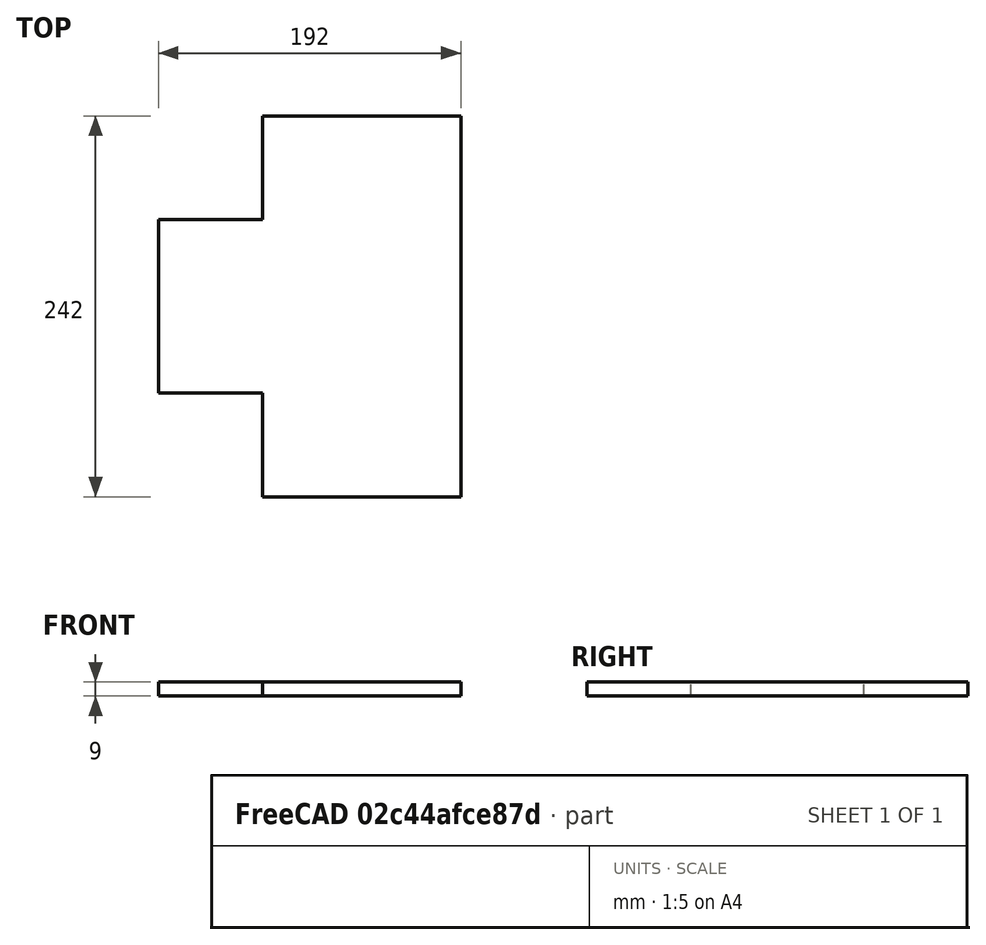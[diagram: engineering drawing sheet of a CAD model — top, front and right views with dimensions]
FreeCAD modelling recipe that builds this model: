
FCSTD DOCUMENT  (FreeCAD 0.16RUnknown)
Label: plaque_bas
License: All rights reserved
LicenseURL: http://en.wikipedia.org/wiki/All_rights_reserved
objects: App::FeaturePython×6, App::DocumentObjectGroup×4, Drawing::FeatureViewPart×4, Part::Plane×3, Drawing::FeatureViewPython×3, Part::Fuse×1, Part::Cut×1, Part::FeaturePython×1, Part::Extrusion×1, Drawing::FeaturePage×1
note: 7 computed .brp shape members not serialized (recipe doc carries the construction recipe); baked Part::Feature solids carry a one-line shape summary decoded from their .brp

FEATURE [Part::Plane] square
  Length = 192
  Placement = pos=(9,-121,0) rot=(0,0,1;0rad)
  Width = 242
FEATURE [Part::Plane] square001
  Length = 75
  Placement = pos=(0,55,0) rot=(0,0,1;0rad)
  Width = 75
FEATURE [Part::Plane] square002
  Length = 75
  Placement = pos=(0,-130,0) rot=(0,0,1;0rad)
  Width = 75
FEATURE [Part::Fuse] union
  Base = -> square001
  Tool = -> square002
FEATURE [Part::Cut] difference
  Base = -> square
  Tool = -> union
FEATURE [Part::FeaturePython] RefineLinearExtrude  # WARN: FeaturePython — macro-defined, semantics opaque (R4)
  Base = -> difference
FEATURE [Part::Extrusion] LinearExtrude
  Base = -> RefineLinearExtrude
  Dir = (0,0,9)
  Solid = true
FEATURE [App::FeaturePython] Dimension  # Draft dimension (typed FeaturePython)
  Dimline = (0,127,0)
  Direction = (0,0,0)
  Distance = 192
  End = (201,121,0)
  Normal = (0,0,1)
  Start = (9,121,0)
FEATURE [App::FeaturePython] Dimension001  # Draft dimension (typed FeaturePython)
  Dimline = (207,0,0)
  Direction = (0,0,0)
  Distance = 242
  End = (201,-121,0)
  Normal = (0,0,1)
  Start = (201,121,0)
FEATURE [App::DocumentObjectGroup] Groupe  label="XY"
  Group = -> [Dimension,Dimension001]
FEATURE [App::FeaturePython] Dimension002  # Draft dimension (typed FeaturePython)
  Dimline = (0,0,15)
  Direction = (0,0,0)
  Distance = 66
  End = (75,0,9)
  Normal = (0,-1,-1.19209e-07)
  Start = (9,0,9)
FEATURE [App::FeaturePython] Dimension003  # Draft dimension (typed FeaturePython)
  Dimline = (0,0,15)
  Direction = (0,0,0)
  Distance = 126
  End = (201,0,9)
  Normal = (0,-1,-1.19209e-07)
  Start = (75,0,9)
FEATURE [App::DocumentObjectGroup] Groupe002  label="XZ"
  Group = -> [Dimension002,Dimension003]
FEATURE [App::FeaturePython] Dimension004  # Draft dimension (typed FeaturePython)
  Dimline = (0,0,15)
  Direction = (0,0,0)
  Distance = 66
  End = (0,55,9)
  Normal = (-1,0,0)
  Start = (0,121,9)
FEATURE [App::FeaturePython] Dimension005  # Draft dimension (typed FeaturePython)
  Dimline = (0,0,15)
  Direction = (0,0,0)
  Distance = 110
  End = (0,-55,9)
  Normal = (-1,0,0)
  Start = (0,55,9)
FEATURE [App::DocumentObjectGroup] Groupe003  label="YZ"
  Group = -> [Dimension004,Dimension005]
FEATURE [App::DocumentObjectGroup] Groupe001  label="Dimensions"
  Group = -> [Groupe,Groupe002,Groupe003]
FEATURE [Drawing::FeatureViewPart] Ortho  label="Ortho_0_0"
  Direction = (1,0,0)
  HiddenWidth = 0.35
  LineWidth = 0.35
  Rotation = -90
  Scale = 0.5
  ShowHiddenLines = true
  ShowSmoothLines = false
  Source = -> LinearExtrude
  Tolerance = 0.05
  ViewResult = <g id="Ortho_0_0"\n   transform="rotate(-90,160,53.33) translate(160,53.33) scale(0.5,0.5)"\n  >\n<g   stroke="rgb(0, 0, 0)"\n   stroke-width="0.7"\n   stroke-linecap="butt"\n   stroke-linejoin="miter"\n   stroke-dasharray="0.2,0.1"\n   fill="none"\n   transform="scale(1,-1)"\n  >\n<path id= "1" d=" M 0 55 L 9 55 " />\n<path id= "2" d=" M 0 -55 L 9 -55 " />\n<path id= "3" d=" M 0 55 L 0 -55 " />\n<path id= "4" d=" M 9 55 L 9 -55 " />\n<path id= "5" d=" M 0 -55 L 9 -55 " />\n<path id= "6" d=" M 0 -121 L 9 -121 " />\n<path id= "7" d=" M 0 -55 L 0 -121 " />\n<path id= "8" d=" M 9 -55 L 9 -121 " />\n<path id= "9" d=" M 0 121 L 9 121 " />\n<path id= "10" d=" M 0 55 L 9 55 " />\n<path id= "11" d=" M 0 121 L 0 55 " />\n<path id= "12" d=" M 9 121 L 9 55 " />\n</g>\n<g   stroke="rgb(0, 0, 0)"\n   stroke-width="0.7"\n   stroke-linecap="butt"\n   stroke-linejoin="miter"\n   fill="none"\n   transform="scale(1,-1)"\n  >\n<path id= "1" d=" M 0 -121 L 9 -121 " />\n<path id= "2" d=" M 0 121 L 9 121 " />\n<path id= "3" d=" M 0 121 L 0 -121 " />\n<path id= "4" d=" M 9 121 L 9 -121 " />\n</g>\n</g>
  Visible = true
  X = 160
  Y = 53.33
FEATURE [Drawing::FeatureViewPart] Ortho002  label="Ortho_-1_0"
  Direction = (0,1,0)
  HiddenWidth = 0.15
  LineWidth = 0.35
  Rotation = 180
  Scale = 0.5
  ShowHiddenLines = false
  ShowSmoothLines = false
  Source = -> LinearExtrude
  Tolerance = 0.05
  ViewResult = <g id="Ortho_-1_0"\n   transform="rotate(180,49.25,87.66) translate(49.25,87.66) scale(0.5,0.5)"\n  >\n<g   stroke="rgb(0, 0, 0)"\n   stroke-width="0.7"\n   stroke-linecap="butt"\n   stroke-linejoin="miter"\n   fill="none"\n   transform="scale(1,-1)"\n  >\n<path id= "1" d=" M 0 9 L 9 9 " />\n<path id= "2" d=" M 0 9 L 0 75 " />\n<path id= "3" d=" M 9 9 L 9 75 " />\n<path id= "4" d=" M 0 75 L 9 75 " />\n<path id= "5" d=" M 0 201 L 9 201 " />\n<path id= "6" d=" M 0 75 L 0 201 " />\n<path id= "7" d=" M 9 75 L 9 201 " />\n</g>\n</g>
  Visible = true
  X = 49.25
  Y = 87.66
FEATURE [Drawing::FeatureViewPart] Ortho003  label="Ortho_1_-1"
  Direction = (0.57735,-0.57735,0.57735)
  HiddenWidth = 0.15
  LineWidth = 0.35
  Rotation = 60
  Scale = 0.5
  ShowHiddenLines = false
  ShowSmoothLines = false
  Source = -> LinearExtrude
  Tolerance = 0.05
  ViewResult = <g id="Ortho_1_-1"\n   transform="rotate(60,275.13,120.571) translate(275.13,120.571) scale(0.5,0.5)"\n  >\n<g   stroke="rgb(0, 0, 0)"\n   stroke-width="0.7"\n   stroke-linecap="butt"\n   stroke-linejoin="miter"\n   fill="none"\n   transform="scale(1,-1)"\n  >\n<path id= "1" d=" M 6.36396 -41.2331 L 0 -37.5588 " />\n<path id= "2" d=" M 0 -37.5588 L 0 52.2558 " />\n<path id= "3" d=" M 0 52.2558 L 46.669 79.2002 " />\n<path id= "4" d=" M 46.669 79.2002 L 46.669 133.089 " />\n<path id= "5" d=" M 142.128 180.854 L 135.765 184.528 " />\n<path id= "6" d=" M 46.669 133.089 L 135.765 184.528 " />\n<path id= "7" d=" M 142.128 -16.7382 L 135.765 -13.0639 " />\n<path id= "8" d=" M 142.128 -16.7382 L 142.128 180.854 " />\n<path id= "9" d=" M 135.765 -13.0639 L 135.765 184.528 " />\n<path id= "10" d=" M 53.033 -68.1775 L 46.669 -64.5032 " />\n<path id= "11" d=" M 53.033 -68.1775 L 142.128 -16.7382 " />\n<path id= "12" d=" M 46.669 -64.5032 L 135.765 -13.0639 " />\n<path id= "13" d=" M 46.669 -64.5032 L 46.669 -10.6145 " />\n<path id= "14" d=" M 6.36396 -41.2331 L 46.669 -17.9629 " />\n<path id= "15" d=" M 0 -37.5588 L 46.669 -10.6145 " />\n</g>\n</g>
  Visible = true
  X = 275.13
  Y = 120.571
FEATURE [Drawing::FeatureViewPart] Ortho004  label="Ortho_0_-1"
  Direction = (0,0,1)
  HiddenWidth = 0.15
  LineWidth = 0.35
  Rotation = 90
  Scale = 0.5
  ShowHiddenLines = false
  ShowSmoothLines = false
  Source = -> LinearExtrude
  Tolerance = 0.05
  ViewResult = <g id="Ortho_0_-1"\n   transform="rotate(90,160,87.6667) translate(160,87.6667) scale(0.5,0.5)"\n  >\n<g   stroke="rgb(0, 0, 0)"\n   stroke-width="0.7"\n   stroke-linecap="butt"\n   stroke-linejoin="miter"\n   fill="none"\n   transform="scale(1,-1)"\n  >\n<path id= "1" d=" M 9 -55 L 9 55 " />\n<path id= "2" d=" M 9 55 L 75 55 " />\n<path id= "3" d=" M 75 55 L 75 121 " />\n<path id= "4" d=" M 75 121 L 201 121 " />\n<path id= "5" d=" M 201 -121 L 201 121 " />\n<path id= "6" d=" M 75 -121 L 201 -121 " />\n<path id= "7" d=" M 75 -121 L 75 -55 " />\n<path id= "8" d=" M 9 -55 L 75 -55 " />\n</g>\n</g>
  Visible = true
  X = 160
  Y = 87.6667
FEATURE [Drawing::FeatureViewPython] ViewGroupe  # drawing view (typed FeaturePython)
  Direction = (0,0,0)
  FillStyle = 0
  FontSize = 12
  LineStyle = 0
  LineWidth = 0.35
  Rotation = 90
  Scale = 0.5
  Source = -> Groupe
  ViewResult = <g id="ViewGroupe" transform="rotate(90.0,160.0,87.67) translate(160.0,87.67) scale(0.5,-0.5)"><path d="M 9.0 121.0 L 9.0 127.0 L 201.0 127.0 L 201.0 121.0" fill="none" stroke="#000000" stroke-width="0.7 px" style="stroke-width:0.7;stroke-miterlimit:4;stroke-dasharray:none" freecad:basepoint1="9.0 121.0" freecad:basepoint2="201.0 121.0" freecad:dimpoint="9.0 127.0"/>\n<path transform="rotate(-0.0,9.0,127.0) translate(9.0,127.0) scale(0.666666666667,0.666666666667)" freecad:skip="1" fill="#000000" stroke="none" style="stroke-miterlimit:4;stroke-dasharray:none" d="M 0 0 L 4 1 L 4 -1 Z"/>\n<path transform="rotate(180.0,201.0,127.0) translate(201.0,127.0) scale(0.666666666667,0.666666666667)" freecad:skip="1" fill="#000000" stroke="none" style="stroke-miterlimit:4;stroke-dasharray:none" d="M 0 0 L 4 1 L 4 -1 Z"/>\n<text fill="#000000" font-size="12.0" style="text-anchor:middle;text-align:center;font-family:" transform="rotate(-0.0,105.0,128.0) translate(105.0,128.0) scale(1,-1) " freecad:skip="1">\n192,00 </text>\n<path d="M 201.0 121.0 L 207.0 121.0 L 207.0 -121.0 L 201.0 -121.0" fill="none" stroke="#000000" stroke-width="0.7 px" style="stroke-width:0.7;stroke-miterlimit:4;stroke-dasharray:none" freecad:basepoint1="201.0 121.0" freecad:basepoint2="201.0 -121.0" freecad:dimpoint="207.0 121.0"/>\n<path transform="rotate(-90.0,207.0,121.0) translate(207.0,121.0) scale(0.666666666667,0.666666666667)" freecad:skip="1" fill="#000000" stroke="none" style="stroke-miterlimit:4;stroke-dasharray:none" d="M 0 0 L 4 1 L 4 -1 Z"/>\n<path transform="rotate(90.0,207.0,-121.0) translate(207.0,-121.0) scale(0.666666666667,0.666666666667)" freecad:skip="1" fill="#000000" stroke="none" style="stroke-miterlimit:4;stroke-dasharray:none" d="M 0 0 L 4 1 L 4 -1 Z"/>\n<text fill="#000000" font-size="12.0" style="text-anchor:middle;text-align:center;font-family:" transform="rotate(-90.0,208.0,0.0) translate(208.0,0.0) scale(1,-1) " freecad:skip="1">\n242,00 </text>\n</g>
  Visible = true
  X = 160
  Y = 87.67
FEATURE [Drawing::FeatureViewPython] ViewGroupe002  # drawing view (typed FeaturePython)
  Direction = (0,0,0)
  FillStyle = 0
  FontSize = 12
  LineStyle = 0
  LineWidth = 0.35
  Rotation = 90
  Scale = 0.5
  Source = -> Groupe002
  ViewResult = <g id="ViewGroupe002" transform="rotate(90.0,46.25,87.66) translate(46.25,87.66) scale(0.5,-0.5)"><path d="M 9.0 0.0 L 9.0 0.0 L 75.0 0.0 L 75.0 0.0" fill="none" stroke="#000000" stroke-width="0.7 px" style="stroke-width:0.7;stroke-miterlimit:4;stroke-dasharray:none" freecad:basepoint1="9.0 0.0" freecad:basepoint2="75.0 0.0" freecad:dimpoint="9.0 0.0"/>\n<path transform="rotate(-0.0,9.0,0.0) translate(9.0,0.0) scale(0.666666666667,0.666666666667)" freecad:skip="1" fill="#000000" stroke="none" style="stroke-miterlimit:4;stroke-dasharray:none" d="M 0 0 L 4 1 L 4 -1 Z"/>\n<path transform="rotate(180.0,75.0,0.0) translate(75.0,0.0) scale(0.666666666667,0.666666666667)" freecad:skip="1" fill="#000000" stroke="none" style="stroke-miterlimit:4;stroke-dasharray:none" d="M 0 0 L 4 1 L 4 -1 Z"/>\n<text fill="#000000" font-size="12.0" style="text-anchor:middle;text-align:center;font-family:" transform="rotate(-0.0,42.0,-1.1920927534e-07) translate(42.0,-1.1920927534e-07) scale(1,-1) " freecad:skip="1">\n66,00 </text>\n<path d="M 75.0 0.0 L 75.0 0.0 L 201.0 0.0 L 201.0 0.0" fill="none" stroke="#000000" stroke-width="0.7 px" style="stroke-width:0.7;stroke-miterlimit:4;stroke-dasharray:none" freecad:basepoint1="75.0 0.0" freecad:basepoint2="201.0 0.0" freecad:dimpoint="75.0 0.0"/>\n<path transform="rotate(-0.0,75.0,0.0) translate(75.0,0.0) scale(0.666666666667,0.666666666667)" freecad:skip="1" fill="#000000" stroke="none" style="stroke-miterlimit:4;stroke-dasharray:none" d="M 0 0 L 4 1 L 4 -1 Z"/>\n<path transform="rotate(180.0,201.0,0.0) translate(201.0,0.0) scale(0.666666666667,0.666666666667)" freecad:skip="1" fill="#000000" stroke="none" style="stroke-miterlimit:4;stroke-dasharray:none" d="M 0 0 L 4 1 L 4 -1 Z"/>\n<text fill="#000000" font-size="12.0" style="text-anchor:middle;text-align:center;font-family:" transform="rotate(-0.0,138.0,-1.1920927534e-07) translate(138.0,-1.1920927534e-07) scale(1,-1) " freecad:skip="1">\n126,00 </text>\n</g>
  Visible = true
  X = 46.25
  Y = 87.66
FEATURE [Drawing::FeatureViewPython] ViewGroupe003  # drawing view (typed FeaturePython)
  Direction = (0,0,0)
  FillStyle = 0
  FontSize = 12
  LineStyle = 0
  LineWidth = 0.35
  Rotation = -90
  Scale = 0.5
  Source = -> Groupe003
  ViewResult = <g id="ViewGroupe003" transform="rotate(-90.0,160.0,51.33) translate(160.0,51.33) scale(0.5,-0.5)"><path d="M 0.0 121.0 L 0.0 121.0 L 0.0 55.0 L 0.0 55.0" fill="none" stroke="#000000" stroke-width="0.7 px" style="stroke-width:0.7;stroke-miterlimit:4;stroke-dasharray:none" freecad:basepoint1="0.0 121.0" freecad:basepoint2="0.0 55.0" freecad:dimpoint="0.0 121.0"/>\n<path transform="rotate(-90.0,0.0,121.0) translate(0.0,121.0) scale(0.666666666667,0.666666666667)" freecad:skip="1" fill="#000000" stroke="none" style="stroke-miterlimit:4;stroke-dasharray:none" d="M 0 0 L 4 1 L 4 -1 Z"/>\n<path transform="rotate(90.0,0.0,55.0) translate(0.0,55.0) scale(0.666666666667,0.666666666667)" freecad:skip="1" fill="#000000" stroke="none" style="stroke-miterlimit:4;stroke-dasharray:none" d="M 0 0 L 4 1 L 4 -1 Z"/>\n<text fill="#000000" font-size="12.0" style="text-anchor:middle;text-align:center;font-family:" transform="rotate(-90.0,0.0,88.0) translate(0.0,88.0) scale(1,-1) " freecad:skip="1">\n66,00 </text>\n<path d="M 0.0 55.0 L 0.0 55.0 L 0.0 -55.0 L 0.0 -55.0" fill="none" stroke="#000000" stroke-width="0.7 px" style="stroke-width:0.7;stroke-miterlimit:4;stroke-dasharray:none" freecad:basepoint1="0.0 55.0" freecad:basepoint2="0.0 -55.0" freecad:dimpoint="0.0 55.0"/>\n<path transform="rotate(-90.0,0.0,55.0) translate(0.0,55.0) scale(0.666666666667,0.666666666667)" freecad:skip="1" fill="#000000" stroke="none" style="stroke-miterlimit:4;stroke-dasharray:none" d="M 0 0 L 4 1 L 4 -1 Z"/>\n<path transform="rotate(90.0,0.0,-55.0) translate(0.0,-55.0) scale(0.666666666667,0.666666666667)" freecad:skip="1" fill="#000000" stroke="none" style="stroke-miterlimit:4;stroke-dasharray:none" d="M 0 0 L 4 1 L 4 -1 Z"/>\n<text fill="#000000" font-size="12.0" style="text-anchor:middle;text-align:center;font-family:" transform="rotate(-90.0,0.0,0.0) translate(0.0,0.0) scale(1,-1) " freecad:skip="1">\n110,00 </text>\n</g>
  Visible = true
  X = 160
  Y = 51.33
FEATURE [Drawing::FeaturePage] Page
  EditableTexts = AUTHOR NAME | CREATION DATE | SUPERVISOR NAME | CHECK DATE | 0,5 | WEIGHT | NUMBER | SHEET | Caisse | Bas
  Group = -> [Ortho,Ortho002,Ortho003,Ortho004,ViewGroupe,ViewGroupe002,ViewGroupe003]
